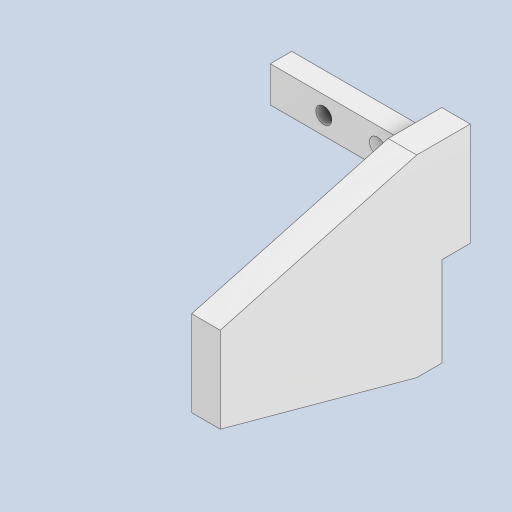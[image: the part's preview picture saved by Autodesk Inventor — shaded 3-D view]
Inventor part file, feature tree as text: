
AUTODESK INVENTOR PART (.ipt)
format: ipt  version: 2023 (Build 270158000, 158)  size: 138,752 bytes
history: native  units: in
note: dims shown in document units (in); Inventor stores cm internally (conversion verified against a paired STEP export)
features: extrude x4, sketch x3
ambient origin geometry x8: Origin, YZ Plane, XZ Plane, XY Plane, X Axis, Y Axis, Z Axis, Center Point
bodies: Body1 (feature_tree)
feature tree (7):
  sketch  "スケッチ2"
  extrude  "押し出し2"  Depth=1.9685in
  extrude  "押し出し5"  Depth=0.3937in
  extrude  "押し出し6"  Depth=0.315in
  extrude  "押し出し7"  Depth=0.1772in
  sketch  "スケッチ4"
  sketch  "スケッチ5"
